# Revit family: Wire_Array-HunterDouglas-V-Baffle_Fins
name_source: partatom
category: Specialty Equipment
revit_build: Autodesk Revit Architecture 2013 (Build: 20120221_2030(x64)
units: mm (PartAtom-declared; Revit-internal decimal feet)

## types (1)
- Parametric
    04 CSI = 09 51 00
    95 CSI = 09510
    Assembly Code = C3030200
    Carrier = Metal - Aluminum Frame - HunterDouglas - Painted White
    Color Finishes = http://www.hunterdouglascontract.com
    Description = Carrier V-Baffle Fins
    Manufacturer = Hunter Douglas Luxalon Metal Ceilings
    Model = V-Baffle Fins
    Panel Spacing = 0' - 6"
    Perforations = http://www.hunterdouglascontract.com
    Product Line = V-Baffle Fins
    Subcategory = Metal Screen Baffle
    URL = http://www.hunterdouglascontract.com
    Wire Hanger = Metal - Aluminum Frame - HunterDouglas - Painted White
    ecoScorecard Product Page = http://hunterdouglascontract.ecoscorecard.com
    ecoScorecard_data = http://products.ecoscorecard.com

## geometry (parser evidence)
native form markers: Sweep x4
no freeform markers — native parametric forms only
